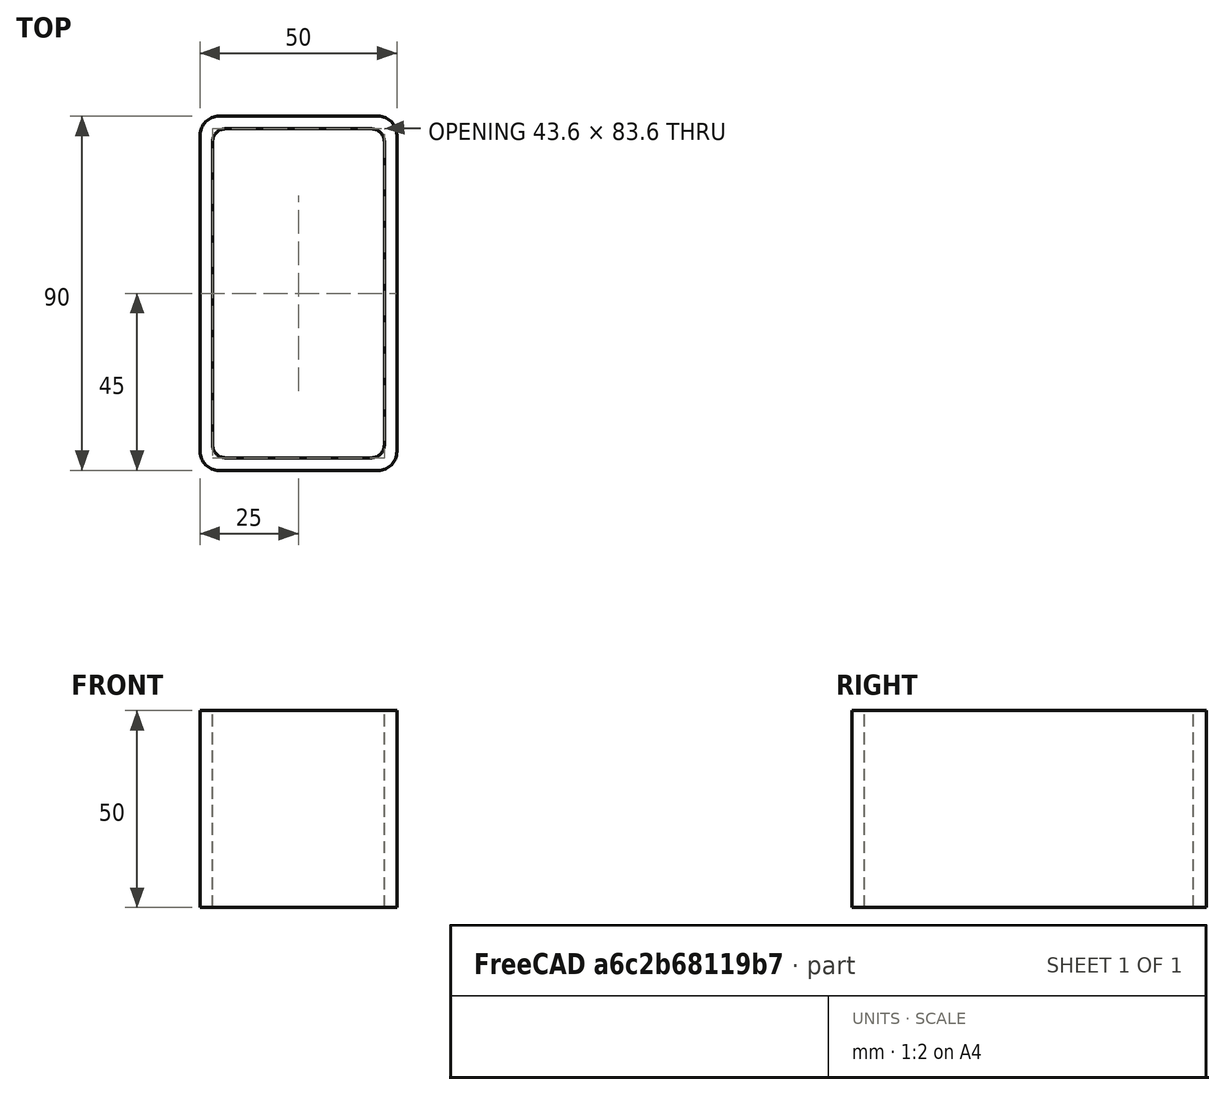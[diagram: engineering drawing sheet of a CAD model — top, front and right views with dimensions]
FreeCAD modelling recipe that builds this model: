
FCSTD DOCUMENT  (FreeCAD 0.15R4671 (Git))
Label: Rectangular hollow section 90x50x3.2 EN10219 S235JRH
License: All rights reserved
LicenseURL: http://en.wikipedia.org/wiki/All_rights_reserved
objects: Sketcher::SketchObject×1, Part::Extrusion×1
note: 2 computed .brp shape members not serialized (recipe doc carries the construction recipe); baked Part::Feature solids carry a one-line shape summary decoded from their .brp

FEATURE [Sketcher::SketchObject] Sketch
  sketch-geometry (16):
    g0: LineSegment StartX=-18.6 StartY=41.8 StartZ=0 EndX=18.6 EndY=41.8 EndZ=0
    g1: LineSegment StartX=21.8 StartY=38.6 StartZ=0 EndX=21.8 EndY=-38.6 EndZ=0
    g2: LineSegment StartX=18.6 StartY=-41.8 StartZ=0 EndX=-18.6 EndY=-41.8 EndZ=0
    g3: LineSegment StartX=-21.8 StartY=-38.6 StartZ=0 EndX=-21.8 EndY=38.6 EndZ=0
    g4: LineSegment StartX=-20.2 StartY=45 StartZ=0 EndX=20.2 EndY=45 EndZ=0
    g5: LineSegment StartX=25 StartY=40.2 StartZ=0 EndX=25 EndY=-40.2 EndZ=0
    g6: LineSegment StartX=20.2 StartY=-45 StartZ=0 EndX=-20.2 EndY=-45 EndZ=0
    g7: LineSegment StartX=-25 StartY=-40.2 StartZ=0 EndX=-25 EndY=40.2 EndZ=0
    g8: ArcOfCircle CenterX=-18.6 CenterY=38.6 CenterZ=0 NormalX=0 NormalY=0 NormalZ=1 Radius=3.2 StartAngle=1.5708 EndAngle=3.14159
    g9: ArcOfCircle CenterX=18.6 CenterY=38.6 CenterZ=0 NormalX=0 NormalY=0 NormalZ=1 Radius=3.2 StartAngle=0 EndAngle=1.5708
    g10: ArcOfCircle CenterX=18.6 CenterY=-38.6 CenterZ=0 NormalX=0 NormalY=0 NormalZ=1 Radius=3.2 StartAngle=4.71239 EndAngle=6.28319
    g11: ArcOfCircle CenterX=-18.6 CenterY=-38.6 CenterZ=0 NormalX=0 NormalY=0 NormalZ=1 Radius=3.2 StartAngle=3.14159 EndAngle=4.71239
    g12: ArcOfCircle CenterX=20.2 CenterY=40.2 CenterZ=0 NormalX=0 NormalY=0 NormalZ=1 Radius=4.8 StartAngle=0 EndAngle=1.5708
    g13: ArcOfCircle CenterX=20.2 CenterY=-40.2 CenterZ=0 NormalX=0 NormalY=0 NormalZ=1 Radius=4.8 StartAngle=4.71239 EndAngle=6.28319
    g14: ArcOfCircle CenterX=-20.2 CenterY=-40.2 CenterZ=0 NormalX=0 NormalY=0 NormalZ=1 Radius=4.8 StartAngle=3.14159 EndAngle=4.71239
    g15: ArcOfCircle CenterX=-20.2 CenterY=40.2 CenterZ=0 NormalX=0 NormalY=0 NormalZ=1 Radius=4.8 StartAngle=1.5708 EndAngle=3.14159
  constraints (36):
    c: Horizontal(g2)
    c: Vertical(g3)
    c: Horizontal(g6)
    c: Vertical(g7)
    c: Tangent(g3,g8) = 1.5708
    c: Tangent(g0,g8) = 1.5708
    c: Tangent(g0,g9) = 1.5708
    c: Tangent(g1,g9) = 1.5708
    c: Tangent(g1,g10) = 1.5708
    c: Tangent(g2,g10) = 1.5708
    c: Tangent(g2,g11) = 1.5708
    c: Tangent(g3,g11) = 1.5708
    c: Tangent(g4,g12) = 1.5708
    c: Tangent(g5,g12) = 1.5708
    c: Tangent(g5,g13) = 1.5708
    c: Tangent(g6,g13) = 1.5708
    c: Tangent(g6,g14) = 1.5708
    c: Tangent(g7,g14) = 1.5708
    c: Tangent(g7,g15) = 1.5708
    c: Tangent(g4,g15) = 1.5708
    c: Equal(g9,g8)
    c: Equal(g9,g11)
    c: Equal(g9,g10)
    c: Equal(g12,g15)
    c: Equal(g12,g14)
    c: Equal(g12,g13)
    c: Symmetric(g4,g6,g-1)
    c: Symmetric(g7,g5,g-2)
    c: DistanceY(g4,g6) = -90
    c: DistanceX(g7,g5) = 50
    c: Symmetric(g3,g1,g-2)
    c: Symmetric(g0,g2,g-1)
    c: DistanceY(g0,g4) = 3.2
    c: DistanceX(g5,g1) = -3.2
    c: Radius(g9) = 3.2
    c: Radius(g12) = 4.8
FEATURE [Part::Extrusion] Extrude  label="Rectangular hollow section 90x50x3.2 EN10219 S235JRH"
  Base = -> Sketch
  Dir = (0,0,50)
  Solid = true
